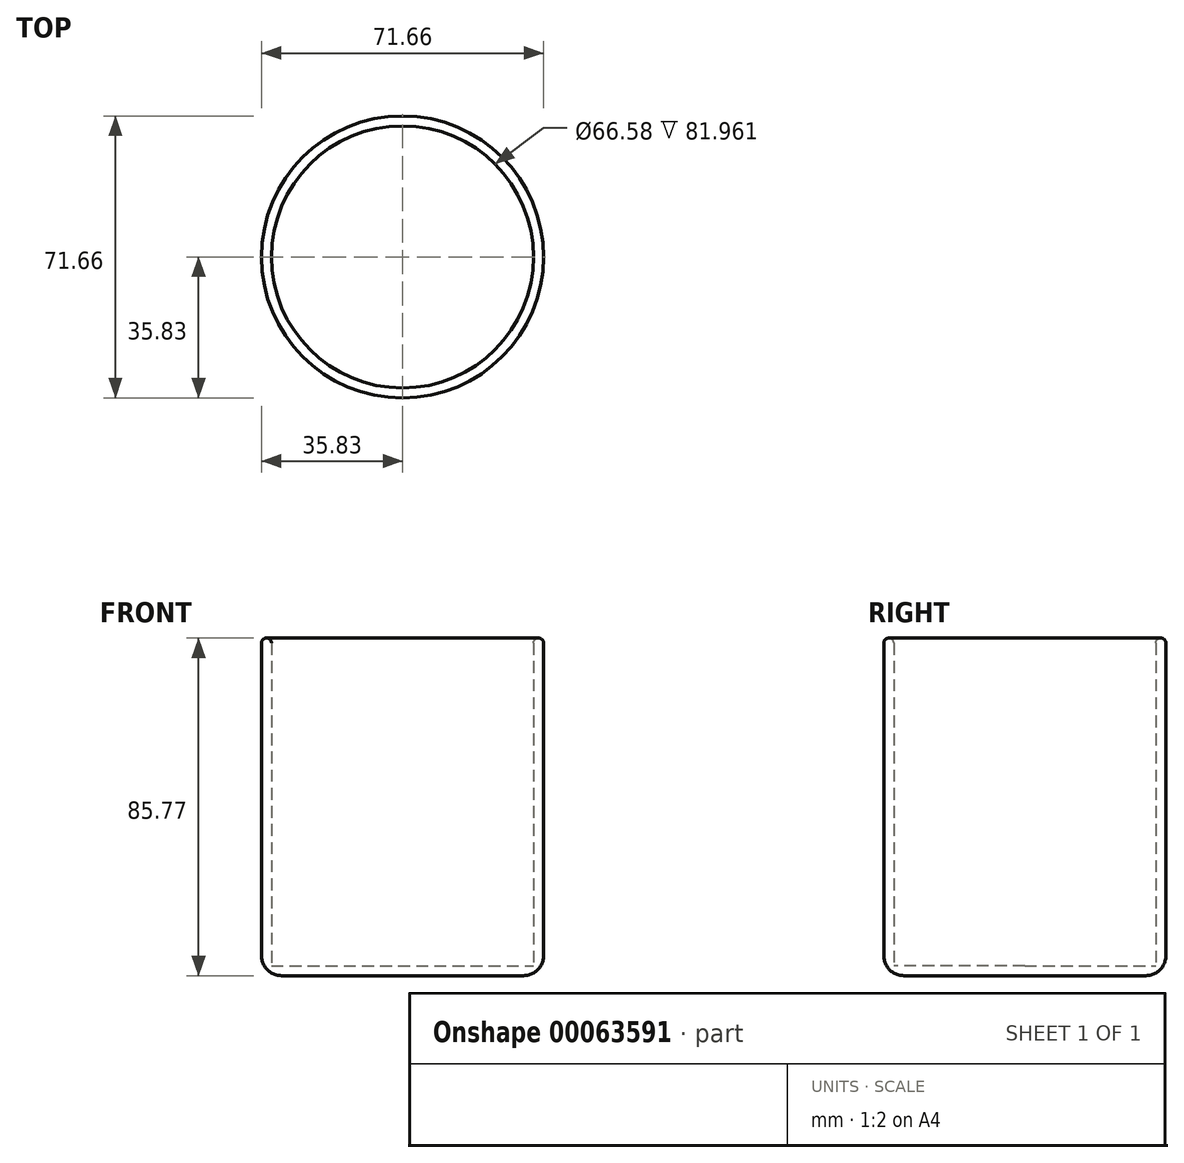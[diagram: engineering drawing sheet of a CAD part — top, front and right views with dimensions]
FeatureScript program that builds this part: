
annotation { "Feature Type Name" : "Feature", "Feature Type Description" : "" }
export const myFeature = defineFeature(function(context is Context, id is Id, definition is map)
    precondition{}
    {
        {
            var Q0;
            Q0=qCreatedBy(makeId("Top.planeOp"),FACE);
            var sketch = newSketch(context, id + "F0", { "sketchPlane" : qUnion([Q0])});
            skCircle(sketch, "E0", {"center": v(0, 0) * mm, "radius": 35.83 * mm});
            skSolve(sketch);
        }
        {
            var Q0;
            Q0=makeQuery(id+"F0.imprint","IMPRINT",FACE,{"disambiguationData":[TD([[makeQuery(id+"F0.imprint","IMPRINT",EDGE,{"derivedFrom":sQuery(id+"F0.wireOp",EDGE,"E0")}),1.0]])]});
            extrude(context, id + "F1", {"entities" : qUnion([Q0]), "depth" : 88.9 * mm});
        }
        {
            var Q0;
            Q0=makeQuery(id+"F1.opExtrude","CAP_FACE",FACE,{"disambiguationData":[OSD([sQuery(id+"F0.wireOp",EDGE,"E0")])],"isStart":false});
            shell(context, id + "F2", {"entities" : qUnion([Q0]), "thickness" : 2.54 * mm});
        }
        {
            var Q0;
            Q0=makeQuery(id+"F1.opExtrude","CAP_EDGE",EDGE,{"disambiguationData":[OSD([sQuery(id+"F0.wireOp",EDGE,"E0")])],"isStart":false});
            var Q1;
            Q1=makeQuery(id+"F1.opExtrude","CAP_EDGE",EDGE,{"disambiguationData":[OSD([sQuery(id+"F0.wireOp",EDGE,"E0")])],"isStart":true});
            fillet(context, id + "F3", {"entities" : qUnion([Q0, Q1]), "radius" : 5.08 * mm, "tangentPropagation" : true, "allowEdgeOverflow" : false});
        }
        {
            var Q0;
            {var subQ0=sQuery(id+"F0.wireOp",EDGE,"E0");Q0=makeQuery(id+"F3.opFillet","BLEND_EDGE",EDGE,{"blendedFrom":[makeQuery(id+"F1.opExtrude","CAP_EDGE",EDGE,{"disambiguationData":[OSD([subQ0])],"isStart":false}),makeQuery(id+"F2.opShell","OFFSET_FACE",FACE,{"disambiguationData":[OSD([subQ0]),TDD([makeQuery(id+"F1.opExtrude","SWEPT_FACE",FACE,{"disambiguationData":[OSD([subQ0])]})])]})],"blendedInto":[makeQuery(id+"F2.opShell","OFFSET_FACE",FACE,{"disambiguationData":[OSD([subQ0]),TDD([makeQuery(id+"F1.opExtrude","SWEPT_FACE",FACE,{"disambiguationData":[OSD([subQ0])]})])]})]});}
            fillet(context, id + "F4", {"entities" : qUnion([Q0]), "radius" : 1.27 * mm, "tangentPropagation" : true, "allowEdgeOverflow" : false});
        }
    });
